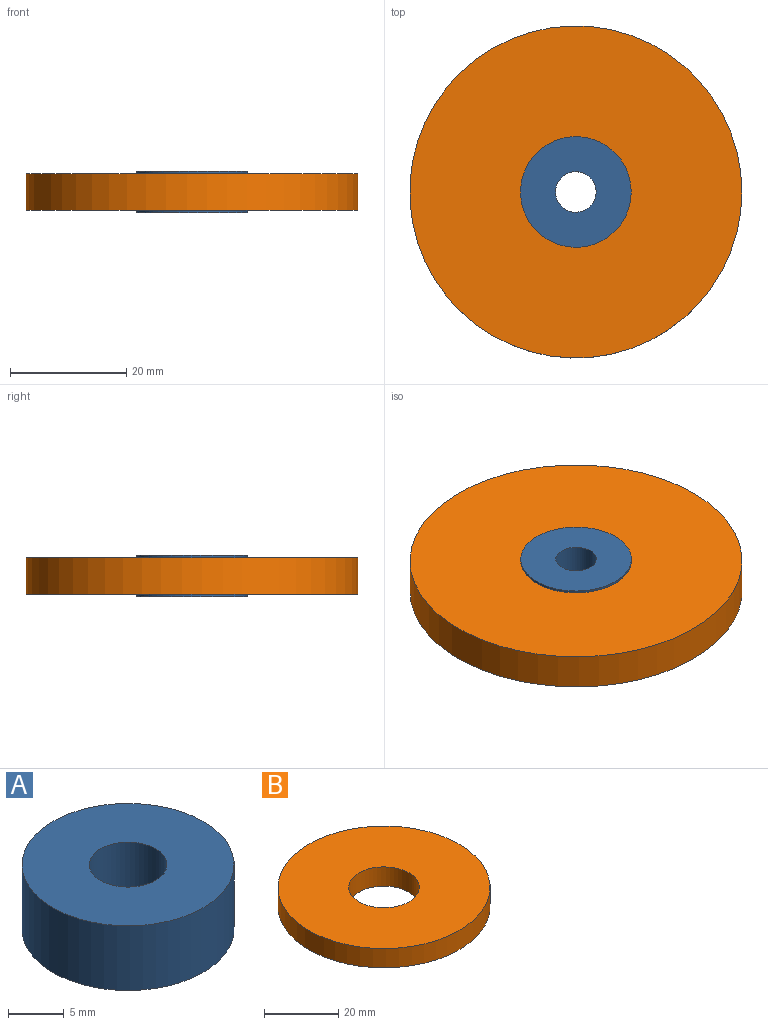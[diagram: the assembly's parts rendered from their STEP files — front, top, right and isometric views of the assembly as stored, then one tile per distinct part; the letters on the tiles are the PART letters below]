
ASSEMBLY  parts=2 mates=1
PART A: 4 faces, bbox 19.1x19.1x7.1 mm
  f0: cylinder r=3.49mm len=7.11mm, axis (0,0,-1), area 156.1mm2, adj f2,f3
  f1: cylinder r=9.53mm len=19.05mm, axis (0,0,-1), area 425.6mm2, adj f2,f3
  f2: plane 19.05x19.05mm, normal (0,0,1), area 246.7mm2, adj f0,f1
  f3: plane 19.05x19.05mm, normal (0,0,-1), area 246.7mm2, adj f0,f1
PART B: 4 faces, bbox 57.2x57.2x6.4 mm
  f0: cylinder r=9.53mm len=19.05mm, axis (0,0,-1), area 380mm2, adj f2,f3
  f1: cylinder r=28.57mm len=57.15mm, axis (0,0,-1), area 1140.1mm2, adj f2,f3
  f2: plane 57.15x57.15mm, normal (0,0,1), area 2280.2mm2, adj f0,f1
  f3: plane 57.15x57.15mm, normal (0,0,-1), area 2280.2mm2, adj f0,f1
PLACE A t=(0,0,-3.56)mm
PLACE B t=(0,0,-3.18)mm
MATE fastened A.f1 <-> B.f1  axis (0,0,-1) through (0,0,0)mm
